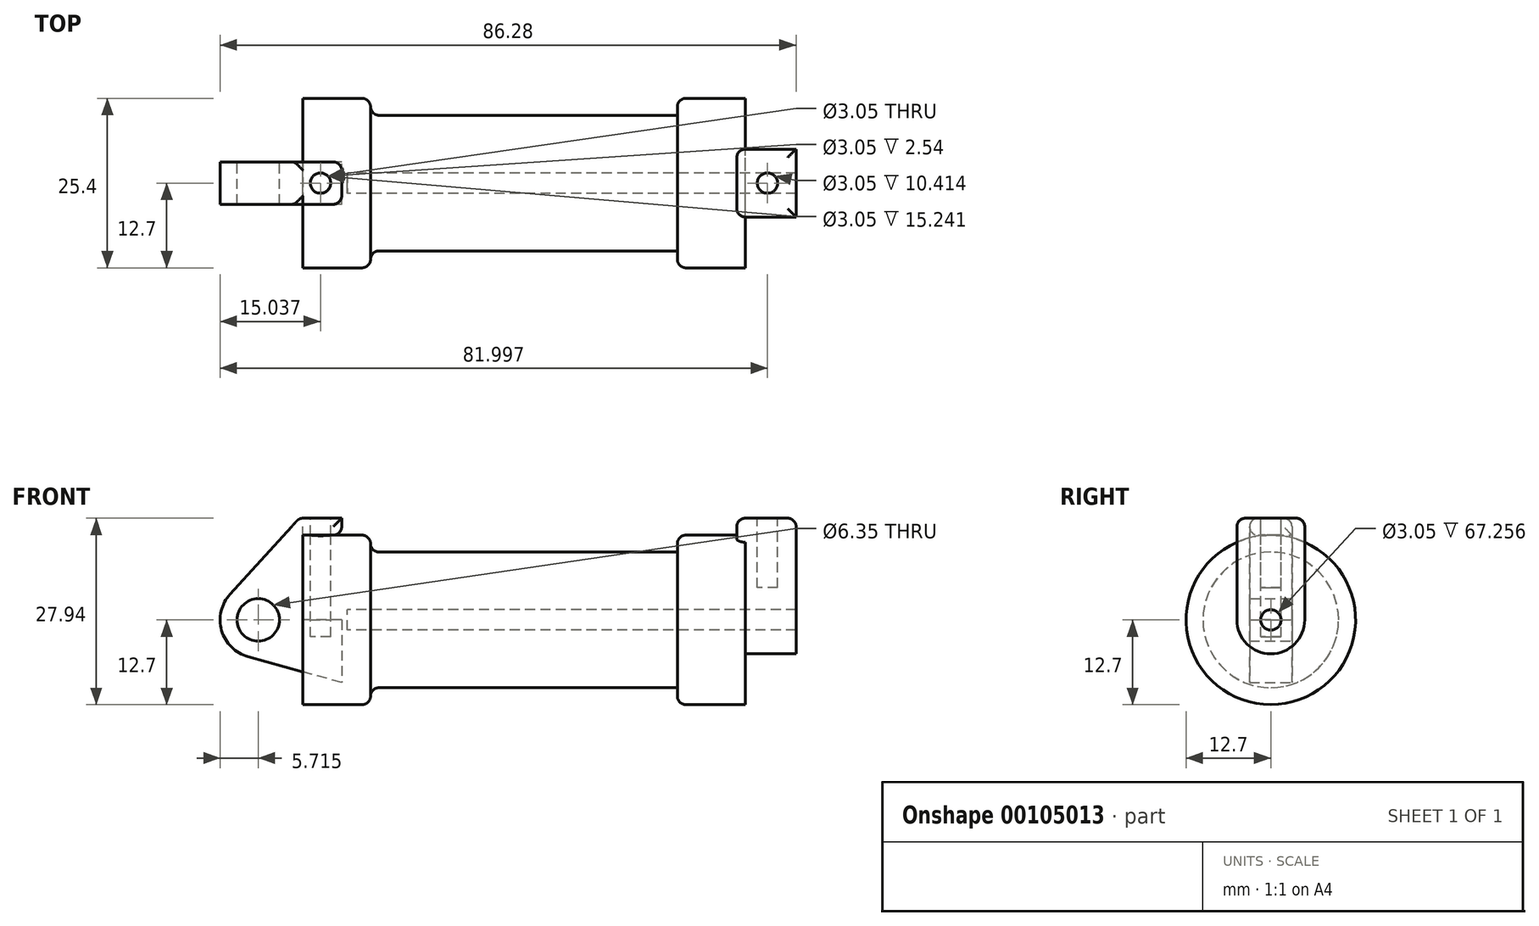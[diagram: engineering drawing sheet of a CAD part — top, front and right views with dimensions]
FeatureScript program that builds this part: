
annotation { "Feature Type Name" : "Feature", "Feature Type Description" : "" }
export const myFeature = defineFeature(function(context is Context, id is Id, definition is map)
    precondition{}
    {
        {
            var Q0;
            Q0=qCreatedBy(makeId("Front.planeOp"),FACE);
            var sketch = newSketch(context, id + "F0", { "sketchPlane" : qUnion([Q0])});
            skLineSegment(sketch, "E0", {"start": v(0, 0) * mm, "end": v(0, 12.7) * mm});
            skLineSegment(sketch, "E1", {"start": v(0, 12.7) * mm, "end": v(10.16, 12.7) * mm});
            skLineSegment(sketch, "E2", {"start": v(10.16, 12.7) * mm, "end": v(10.16, 10.16) * mm});
            skLineSegment(sketch, "E3", {"start": v(10.16, 10.16) * mm, "end": v(56.13, 10.16) * mm});
            skLineSegment(sketch, "E4", {"start": v(56.13, 10.16) * mm, "end": v(56.13, 12.7) * mm});
            skLineSegment(sketch, "E5", {"start": v(56.13, 12.7) * mm, "end": v(66.3, 12.7) * mm});
            skLineSegment(sketch, "E6", {"start": v(66.3, 12.7) * mm, "end": v(66.3, 0) * mm});
            skLineSegment(sketch, "E7", {"start": v(66.3, 0) * mm, "end": v(0, 0) * mm});
            skLineSegment(sketch, "E8", {"start": v(5.84, 15.24) * mm, "end": v(-0.5, 15.24) * mm});
            skLineSegment(sketch, "E9", {"start": v(-0.5, 15.24) * mm, "end": v(-10.88, 3.85) * mm});
            skLineSegment(sketch, "E10", {"start": v(0, 0) * mm, "end": v(-6.65, 0) * mm});
            skCircle(sketch, "E11", {"center": v(-6.65, 0) * mm, "radius": 5.72 * mm});
            skCircle(sketch, "E12", {"center": v(-6.65, 0) * mm, "radius": 3.18 * mm});
            skLineSegment(sketch, "E13", {"start": v(5.84, 15.24) * mm, "end": v(5.84, -9.4) * mm});
            skLineSegment(sketch, "E14", {"start": v(5.84, -9.4) * mm, "end": v(-8.18, -5.5) * mm});
            skSolve(sketch);
        }
        {
            var Q0;
            {var subQ0=sQuery(id+"F0.wireOp",EDGE,"E2");Q0=makeQuery(id+"F0.imprint","IMPRINT",FACE,{"disambiguationData":[TD([[makeQuery(id+"F0.imprint","IMPRINT",EDGE,{"derivedFrom":subQ0}),-1.0]])]});}
            var Q1;
            Q1=sQuery(id+"F0.wireOp",EDGE,"E7");
            revolve(context, id + "F1", {"entities" : qUnion([Q0]), "axis" : qUnion([Q1]), "revolveType" : RevolveType.FULL});
        }
        {
            var Q0;
            {var subQ0=sQuery(id+"F0.wireOp",EDGE,"E0");Q0=makeQuery(id+"F0.imprint","IMPRINT",FACE,{"disambiguationData":[TD([[makeQuery(id+"F0.imprint","IMPRINT",EDGE,{"derivedFrom":subQ0}),-1.0]])]});}
            var Q1;
            Q1=sQuery(id+"F0.wireOp",EDGE,"E7");
            revolve(context, id + "F2", {"operationType" : NewBodyOperationType.ADD, "entities" : qUnion([Q0]), "axis" : qUnion([Q1]), "revolveType" : RevolveType.FULL});
        }
        {
            var Q0;
            {var subQ4=sQuery(id+"F0.wireOp",EDGE,"E12");Q0=makeQuery(id+"F0.imprint","IMPRINT",FACE,{"disambiguationData":[TD([[makeQuery(id+"F0.imprint","IMPRINT",EDGE,{"derivedFrom":subQ4}),-1.0]])]});}
            var Q1;
            {var subQ0=sQuery(id+"F0.wireOp",EDGE,"E14");Q1=makeQuery(id+"F0.imprint","IMPRINT",FACE,{"disambiguationData":[TD([[makeQuery(id+"F0.imprint","IMPRINT",EDGE,{"derivedFrom":subQ0}),-1.0]])]});}
            var Q2;
            {var subQ3=sQuery(id+"F0.wireOp",EDGE,"E0");Q2=makeQuery(id+"F0.imprint","IMPRINT",FACE,{"disambiguationData":[TD([[makeQuery(id+"F0.imprint","IMPRINT",EDGE,{"derivedFrom":subQ3}),1.0]])]});}
            extrude(context, id + "F3", {"entities" : qUnion([Q0, Q1, Q2]), "endBound" : BoundingType.SYMMETRIC, "depth" : 6.35 * mm});
        }
        {
            var Q0;
            Q0=makeQuery(id+"F1.opRevolve","SWEPT_FACE",FACE,{"disambiguationData":[OSD([sQuery(id+"F0.wireOp",EDGE,"E6")])]});
            var sketch = newSketch(context, id + "F4", { "sketchPlane" : qUnion([Q0])});
            skCircle(sketch, "E15", {"center": v(0, 0) * mm, "radius": 1.52 * mm});
            skCircle(sketch, "E16", {"center": v(0, 0) * mm, "radius": 5.08 * mm});
            skLineSegment(sketch, "E17", {"start": v(5.08, 0) * mm, "end": v(5.08, 15.24) * mm});
            skLineSegment(sketch, "E18", {"start": v(-5.08, 0) * mm, "end": v(-5.08, 15.24) * mm});
            skLineSegment(sketch, "E19", {"start": v(-5.08, 15.24) * mm, "end": v(5.08, 15.24) * mm});
            skSolve(sketch);
        }
        {
            var Q0;
            {var subQ0=sQuery(id+"F4.wireOp",EDGE,"E17");var subQ1=sQuery(id+"F4.wireOp",EDGE,"E16");var subQ2=makeQuery(id+"F4.imprint","INTERSECT",VERTEX,{"derivedFrom":[subQ1,subQ0]});Q0=makeQuery(id+"F4.imprint","IMPRINT",FACE,{"disambiguationData":[TD([[makeQuery(id+"F4.imprint","IMPRINT",EDGE,{"disambiguationData":[TD([[subQ2,-1.0]])],"derivedFrom":subQ1}),-1.0]])]});}
            var Q1;
            Q1=makeQuery(id+"F4.imprint","IMPRINT",FACE,{"disambiguationData":[TD([[makeQuery(id+"F4.imprint","IMPRINT",EDGE,{"derivedFrom":sQuery(id+"F4.wireOp",EDGE,"E15")}),-1.0]])]});
            extrude(context, id + "F5", {"entities" : qUnion([Q0, Q1]), "operationType" : NewBodyOperationType.ADD, "depth" : 7.62 * mm});
        }
        {
            var Q0;
            {var subQ0=sQuery(id+"F4.wireOp",EDGE,"E19");Q0=makeQuery(id+"F4.imprint","IMPRINT",FACE,{"disambiguationData":[TD([[makeQuery(id+"F4.imprint","IMPRINT",EDGE,{"derivedFrom":subQ0}),-1.0]])]});}
            extrude(context, id + "F6", {"entities" : qUnion([Q0]), "operationType" : NewBodyOperationType.ADD, "depth" : 7.62 * mm});
        }
        {
            var Q0;
            Q0=makeQuery(id+"F6.opExtrude","CAP_FACE",FACE,{"disambiguationData":[OSD([sQuery(id+"F0.wireOp",EDGE,"E5"),sQuery(id+"F0.wireOp",EDGE,"E6"),sQuery(id+"F4.wireOp",EDGE,"E17"),sQuery(id+"F4.wireOp",EDGE,"E18"),sQuery(id+"F4.wireOp",EDGE,"E19")])],"isStart":true});
            extrude(context, id + "F7", {"entities" : qUnion([Q0]), "operationType" : NewBodyOperationType.ADD, "depth" : 1.27 * mm});
        }
        {
            var Q0;
            Q0=makeQuery(id+"F4.imprint","IMPRINT",FACE,{"disambiguationData":[TD([[makeQuery(id+"F4.imprint","IMPRINT",EDGE,{"derivedFrom":sQuery(id+"F4.wireOp",EDGE,"E15")}),1.0]])]});
            extrude(context, id + "F8", {"entities" : qUnion([Q0]), "operationType" : NewBodyOperationType.REMOVE, "oppositeDirection" : true, "depth" : 59.64 * mm});
        }
        {
            var Q0;
            {var subQ0=sQuery(id+"F4.wireOp",EDGE,"E19");Q0=makeQuery(id+"F7.boolean.opBoolean","MERGE",FACE,{"derivedFrom":[makeQuery(id+"F6.opExtrude","SWEPT_FACE",FACE,{"disambiguationData":[OSD([subQ0])]}),makeQuery(id+"F7.opExtrude","SWEPT_FACE",FACE,{"disambiguationData":[OSD([subQ0])]})]});}
            var sketch = newSketch(context, id + "F9", { "sketchPlane" : qUnion([Q0])});
            skLineSegment(sketch, "E20", {"start": v(65.02, 0) * mm, "end": v(73.91, 0) * mm, "construction": true});
            skLineSegment(sketch, "E21", {"start": v(69.63, -5.08) * mm, "end": v(69.63, 5.08) * mm, "construction": true});
            skCircle(sketch, "E22", {"center": v(69.63, 0) * mm, "radius": 1.52 * mm});
            skSolve(sketch);
        }
        {
            var Q0;
            Q0 = qSketchRegion(id + "F9", true);
            extrude(context, id + "F10", {"entities" : qUnion([Q0]), "operationType" : NewBodyOperationType.REMOVE, "oppositeDirection" : true, "depth" : 10.4 * mm});
        }
        {
            var Q0;
            Q0=makeQuery(id+"F3.opExtrude","SWEPT_FACE",FACE,{"disambiguationData":[OSD([sQuery(id+"F0.wireOp",EDGE,"E8")])]});
            var sketch = newSketch(context, id + "F11", { "sketchPlane" : qUnion([Q0])});
            skLineSegment(sketch, "E23", {"start": v(2.67, 3.18) * mm, "end": v(2.67, -3.18) * mm, "construction": true});
            skLineSegment(sketch, "E24", {"start": v(-0.5, 0) * mm, "end": v(5.84, 0) * mm, "construction": true});
            skCircle(sketch, "E25", {"center": v(2.67, 0) * mm, "radius": 1.52 * mm});
            skSolve(sketch);
        }
        {
            var Q0;
            Q0 = qSketchRegion(id + "F11", true);
            extrude(context, id + "F12", {"entities" : qUnion([Q0]), "operationType" : NewBodyOperationType.REMOVE, "oppositeDirection" : true, "depth" : 17.78 * mm});
        }
        {
            var Q0;
            Q0=makeQuery(id+"F3.opExtrude","CAP_EDGE",EDGE,{"disambiguationData":[OSD([sQuery(id+"F0.wireOp",EDGE,"E8")])],"isStart":false});
            var Q1;
            Q1=makeQuery(id+"F3.opExtrude","CAP_EDGE",EDGE,{"disambiguationData":[OSD([sQuery(id+"F0.wireOp",EDGE,"E1")])],"isStart":false});
            var Q2;
            Q2=makeQuery(id+"F3.opExtrude","SWEPT_EDGE",EDGE,{"disambiguationData":[OSD([sQuery(id+"F0.wireOp",EDGE,"E1"),sQuery(id+"F0.wireOp",EDGE,"E13")])]});
            var Q3;
            {var subQ0=sQuery(id+"F0.wireOp",EDGE,"E13");Q3=makeQuery(id+"F3.opExtrude","CAP_EDGE",EDGE,{"disambiguationData":[OSD([subQ0]),TDD([makeQuery(id+"F0.imprint","IMPRINT",EDGE,{"disambiguationData":[TD([[makeQuery(id+"F0.imprint","INTERSECT",VERTEX,{"derivedFrom":[sQuery(id+"F0.wireOp",EDGE,"E8"),subQ0]}),-1.0]])],"derivedFrom":subQ0})])],"isStart":true});}
            var Q4;
            Q4=makeQuery(id+"F3.opExtrude","CAP_EDGE",EDGE,{"disambiguationData":[OSD([sQuery(id+"F0.wireOp",EDGE,"E8")])],"isStart":true});
            var Q5;
            Q5=makeQuery(id+"F3.opExtrude","SWEPT_EDGE",EDGE,{"disambiguationData":[OSD([sQuery(id+"F0.wireOp",EDGE,"E8"),sQuery(id+"F0.wireOp",EDGE,"E9")])]});
            var Q6;
            Q6=makeQuery(id+"F1.opRevolve","SWEPT_FACE",FACE,{"disambiguationData":[OSD([sQuery(id+"F0.wireOp",EDGE,"E2")])]});
            var Q7;
            Q7=makeQuery(id+"F1.opRevolve","SWEPT_EDGE",EDGE,{"disambiguationData":[OSD([sQuery(id+"F0.wireOp",EDGE,"E4"),sQuery(id+"F0.wireOp",EDGE,"E5")])]});
            var Q8;
            Q8=makeQuery(id+"F7.opExtrude","CAP_EDGE",EDGE,{"disambiguationData":[OSD([sQuery(id+"F4.wireOp",EDGE,"E18")])],"isStart":false});
            var Q9;
            Q9=makeQuery(id+"F7.opExtrude","CAP_EDGE",EDGE,{"disambiguationData":[OSD([sQuery(id+"F4.wireOp",EDGE,"E19")])],"isStart":false});
            var Q10;
            Q10=makeQuery(id+"F7.opExtrude","CAP_EDGE",EDGE,{"disambiguationData":[OSD([sQuery(id+"F0.wireOp",EDGE,"E5"),sQuery(id+"F0.wireOp",EDGE,"E6")])],"isStart":false});
            var Q11;
            Q11=makeQuery(id+"F7.opExtrude","CAP_EDGE",EDGE,{"disambiguationData":[OSD([sQuery(id+"F4.wireOp",EDGE,"E17")])],"isStart":false});
            var Q12;
            {var subQ0=sQuery(id+"F4.wireOp",EDGE,"E19");var subQ1=sQuery(id+"F4.wireOp",EDGE,"E18");Q12=makeQuery(id+"F7.boolean.opBoolean","MERGE",EDGE,{"derivedFrom":[makeQuery(id+"F6.opExtrude","SWEPT_EDGE",EDGE,{"disambiguationData":[OSD([subQ1,subQ0])]}),makeQuery(id+"F7.opExtrude","SWEPT_EDGE",EDGE,{"disambiguationData":[OSD([subQ1,subQ0])]})]});}
            var Q13;
            Q13=makeQuery(id+"F6.opExtrude","CAP_EDGE",EDGE,{"disambiguationData":[OSD([sQuery(id+"F4.wireOp",EDGE,"E19")])],"isStart":false});
            var Q14;
            {var subQ0=sQuery(id+"F4.wireOp",EDGE,"E19");var subQ1=sQuery(id+"F4.wireOp",EDGE,"E17");Q14=makeQuery(id+"F7.boolean.opBoolean","MERGE",EDGE,{"derivedFrom":[makeQuery(id+"F6.opExtrude","SWEPT_EDGE",EDGE,{"disambiguationData":[OSD([subQ1,subQ0])]}),makeQuery(id+"F7.opExtrude","SWEPT_EDGE",EDGE,{"disambiguationData":[OSD([subQ1,subQ0])]})]});}
            var Q15;
            {var subQ0=sQuery(id+"F0.wireOp",EDGE,"E13");Q15=makeQuery(id+"F3.opExtrude","CAP_EDGE",EDGE,{"disambiguationData":[OSD([subQ0]),TDD([makeQuery(id+"F0.imprint","IMPRINT",EDGE,{"disambiguationData":[TD([[makeQuery(id+"F0.imprint","INTERSECT",VERTEX,{"derivedFrom":[sQuery(id+"F0.wireOp",EDGE,"E8"),subQ0]}),-1.0]])],"derivedFrom":subQ0})])],"isStart":false});}
            fillet(context, id + "F13", {"entities" : qUnion([Q0, Q1, Q2, Q3, Q4, Q5, Q6, Q7, Q8, Q9, Q10, Q11, Q12, Q13, Q14, Q15]), "radius" : 1.27 * mm, "tangentPropagation" : true, "allowEdgeOverflow" : false});
        }
    });
